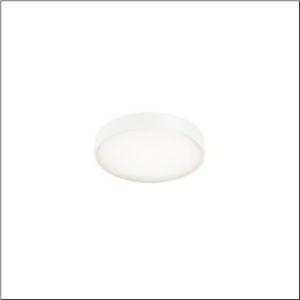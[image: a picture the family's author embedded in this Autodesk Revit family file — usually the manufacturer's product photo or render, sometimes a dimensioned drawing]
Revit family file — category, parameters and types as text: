
# Revit family: round_21_s_51mr34fd0421w
name_source: partatom
category: Lighting Fixtures
units: mm (PartAtom-declared; Revit-internal decimal feet)

## family parameters
Cut with Voids When Loaded = No
Host = Face
Light Source = No
Part Type = Normal
Room Calculation Point = No
Round Connector Dimension = Use Diameter
Shared = No

## types (1)
- Round 21 S (1 x LED, 3910 lm, 30.3 W, 4000K)
    Apparent Load = 30 VA
    CIE Flux Codes = 49 80 96 100 100
    Color Rendering = 80
    Color Temperature = 4000K
    Default Elevation = 1800 mm
    Description = Round 21 S, wall and ceiling luminaire, primary optical cover: cover, of PMMA, opal, light emission: direct distribution, primary light characteristic: symmetric, installation type: suspended mounting, surface-mounted, LED, rated luminous flux: 3.900lm, luminous efficacy: 129lm/W, light colour: 840, colour temperature: 4000K, control gear: DALI 2, with terminal, 5-pole, mains connection: 230V, AC, 50/60Hz, rated input power: 30.3W, housing, of aluminium, coated, white, diameter: 400mm, height: 62mm, protection rating (complete): IP40, insulation class (complete): insulation class I (protective earthing), certification: CE, impact resistance: IK04, permissible operating ambient temperature: -10..+35°C, packaging unit: 1 piece
    Height = 87 mm
    Lamp = 1 x LED
    Lamp Light Flux = 3910 lm
    Lamp Power = 30.3 W
    Lamp count = 1
    Length = 400 mm
    Luminous efficacy = 129 lm/W
    Manufacturer = Siteco
    ModVariant = No
    Model = 51MR34FD0421W
    Mounting Place = Ceiling
    Mounting Type = Surface mounted
    Number of Poles = 1
    OnlyDefault = Yes
    Power Factor = 1
    Product Name = Round 21 S
    Product group = wall and ceiling luminaire
    ProductGroupID = 304
    Protection Class = Protection class I
    Protection Degree = IP 40
    RLX_Detail_Level = 1
    RLX_Emergency_Light_Flux = 0 lm
    RLX_Emergency_Type = 0
    RLX_Emergency_Type_DB = No
    RlxData = <blob elided: 9513 chars, md5=a7a42c3c>
    Socket = socket
    Standby Power = 0 W
    System Light Flux = 3910 lm
    System Power = 30 W
    Type Comments = Product without accessories
    Type Image = l_1258307.jpg
    URL = http://relux.com
    VarID = ---
    Voltage = 0 V
    Weight = 0.00 kg
    Width = 0 mm  [stored 0 ft]

note: [stored X ft] marks values corroborated as IEEE doubles in the binary element streams (Revit-internal decimal feet)

## geometry (parser evidence)
native form markers: Sweep x7
no freeform markers — native parametric forms only
